# Revit family: Точечный зенитный фонарь (люк) M8CITY_П_2017_revit
name_source: partatom
category: Окна
revit_build: Autodesk Revit 2017 (Build: 20170118_1100(x64)
units: mm (PartAtom-declared; Revit-internal decimal feet)

## family parameters
Всегда вертикально = Нет
Общий = Нет
Основа = Крыша
При загрузке вырезать с полостями = Нет
Точка расчета площади = Нет

## types (1)
- Зенитный фонарь M8CITY Т-П-pro
    ADSK_Завод-изготовитель = ООО ''Завод М8 Сити''
    ADSK_Код изделия = ТУ BY 191302027.002-2013
    ADSK_Количество = 1
    ADSK_Обозначение = M8CITY
    ADSK_Размер_Высота = 300 мм
    ADSK_Размер_Длина = 800 мм
    ADSK_Размер_Ширина = 800 мм
    Table 1 = Описание
    Table 2 = Расчет
    Table 3 = Маркировка
    URL = www.m8city.by
    Высота = 373 мм
    Высота основания = 300 мм
    Длина = 800 мм
    Длина проёма = 800 мм
    Длина проёма ввод = 800 мм
    Заполнение = 3
    ПМ16 = Створка : ПК молочный 16 мм
    ПМ20 = Створка : ПК молочный 20 мм
    ПП16 = Створка : ПК прозрачный 16 мм
    ПП20 = Створка : ПК прозрачный 20 мм
    Привод = 3
    СП26 = Створка : СП 26 мм
    Ширина = 800 мм
    Ширина проёма = 800 мм
    Ширина проёма ввод = 800 мм
